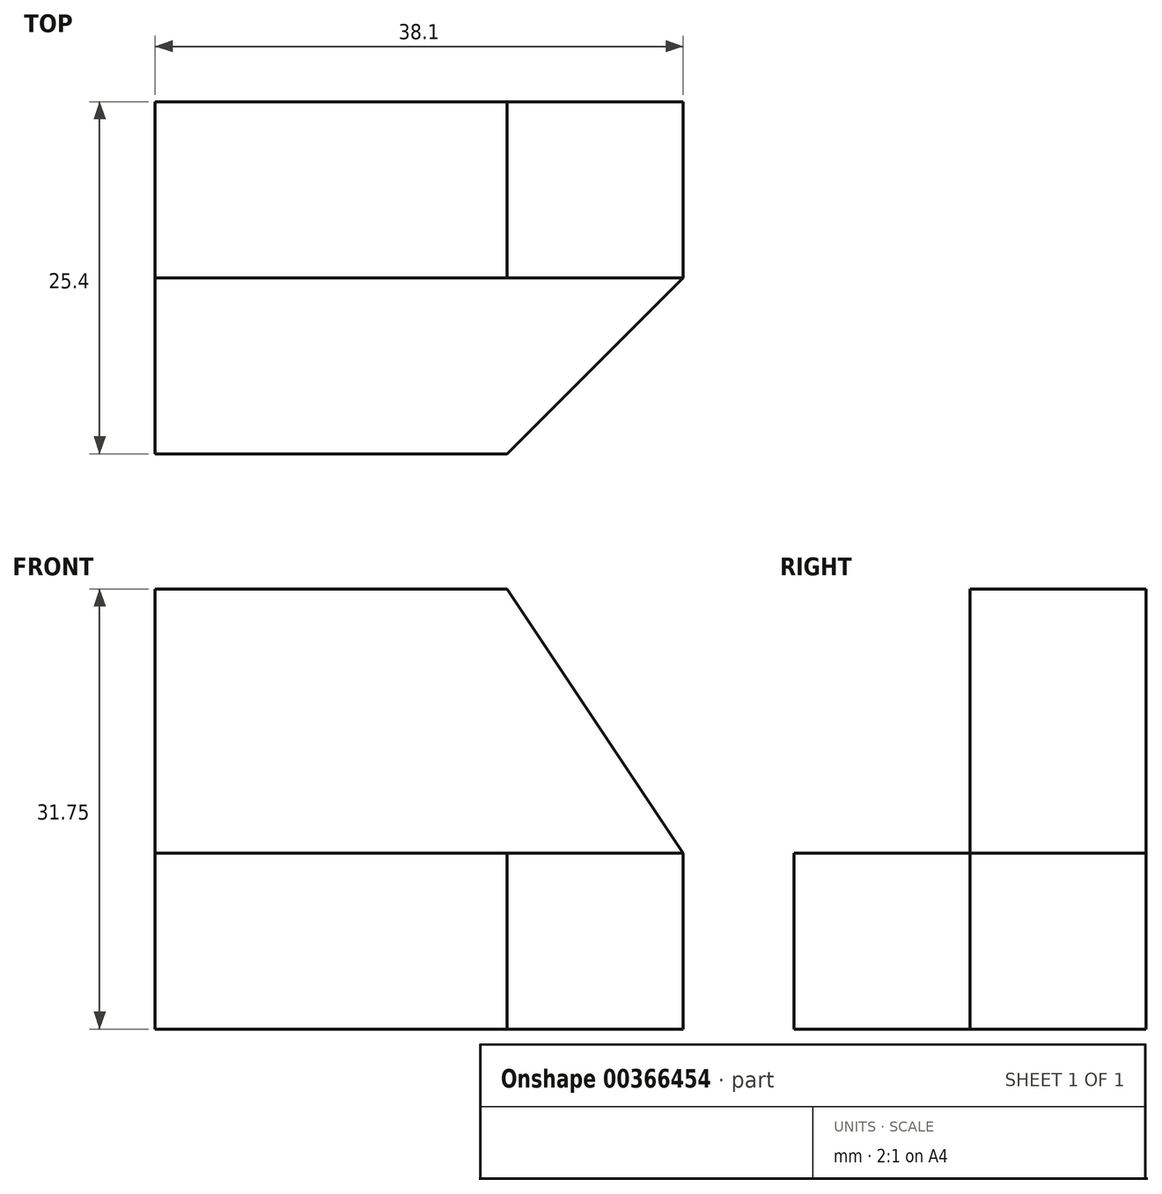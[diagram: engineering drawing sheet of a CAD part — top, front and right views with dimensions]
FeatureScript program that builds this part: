
annotation { "Feature Type Name" : "Feature", "Feature Type Description" : "" }
export const myFeature = defineFeature(function(context is Context, id is Id, definition is map)
    precondition{}
    {
        {
            var Q0;
            Q0=qCreatedBy(makeId("Right.planeOp"),FACE);
            var sketch = newSketch(context, id + "F0", { "sketchPlane" : qUnion([Q0])});
            skLineSegment(sketch, "E0", {"start": v(0, 0) * mm, "end": v(-25.4, 0) * mm});
            skLineSegment(sketch, "E1", {"start": v(-25.4, 0) * mm, "end": v(-25.4, 12.7) * mm});
            skLineSegment(sketch, "E2", {"start": v(-25.4, 12.7) * mm, "end": v(-12.7, 12.7) * mm});
            skLineSegment(sketch, "E3", {"start": v(-12.7, 12.7) * mm, "end": v(-12.7, 31.75) * mm});
            skLineSegment(sketch, "E4", {"start": v(-12.7, 31.75) * mm, "end": v(0, 31.75) * mm});
            skLineSegment(sketch, "E5", {"start": v(0, 31.75) * mm, "end": v(0, 0) * mm});
            skSolve(sketch);
        }
        {
            var Q0;
            Q0 = qSketchRegion(id + "F0", true);
            extrude(context, id + "F1", {"entities" : qUnion([Q0]), "depth" : 38.1 * mm});
        }
        {
            var Q0;
            Q0=makeQuery(id+"F1.opExtrude","SWEPT_FACE",FACE,{"disambiguationData":[OSD([sQuery(id+"F0.wireOp",EDGE,"E3")])]});
            var sketch = newSketch(context, id + "F2", { "sketchPlane" : qUnion([Q0])});
            skLineSegment(sketch, "E6", {"start": v(0, 31.75) * mm, "end": v(25.4, 31.75) * mm});
            skLineSegment(sketch, "E7", {"start": v(25.4, 31.75) * mm, "end": v(38.1, 12.7) * mm});
            skLineSegment(sketch, "E8", {"start": v(38.1, 12.7) * mm, "end": v(38.1, 31.75) * mm});
            skLineSegment(sketch, "E9", {"start": v(38.1, 31.75) * mm, "end": v(25.4, 31.75) * mm});
            skSolve(sketch);
        }
        {
            var Q0;
            Q0 = qSketchRegion(id + "F2", true);
            extrude(context, id + "F3", {"entities" : qUnion([Q0]), "operationType" : NewBodyOperationType.REMOVE, "oppositeDirection" : true, "depth" : 25.4 * mm});
        }
        {
            var Q0;
            Q0=makeQuery(id+"F1.opExtrude","SWEPT_FACE",FACE,{"disambiguationData":[OSD([sQuery(id+"F0.wireOp",EDGE,"E2")])]});
            var sketch = newSketch(context, id + "F4", { "sketchPlane" : qUnion([Q0])});
            skLineSegment(sketch, "E10", {"start": v(0, -25.4) * mm, "end": v(25.4, -25.4) * mm});
            skLineSegment(sketch, "E11", {"start": v(25.4, -25.4) * mm, "end": v(38.1, -12.7) * mm});
            skSolve(sketch);
        }
        {
            var Q0;
            Q0 = qSketchRegion(id + "F4", true);
            var Q1;
            {var subQ0=sQuery(id+"F4.wireOp",EDGE,"E11");Q1=makeQuery(id+"F4.imprint","IMPRINT",FACE,{"disambiguationData":[TD([[makeQuery(id+"F4.imprint","IMPRINT",EDGE,{"derivedFrom":subQ0}),-1.0]])]});}
            extrude(context, id + "F5", {"entities" : qUnion([Q0, Q1]), "operationType" : NewBodyOperationType.REMOVE, "oppositeDirection" : true, "depth" : 25.4 * mm});
        }
    });
